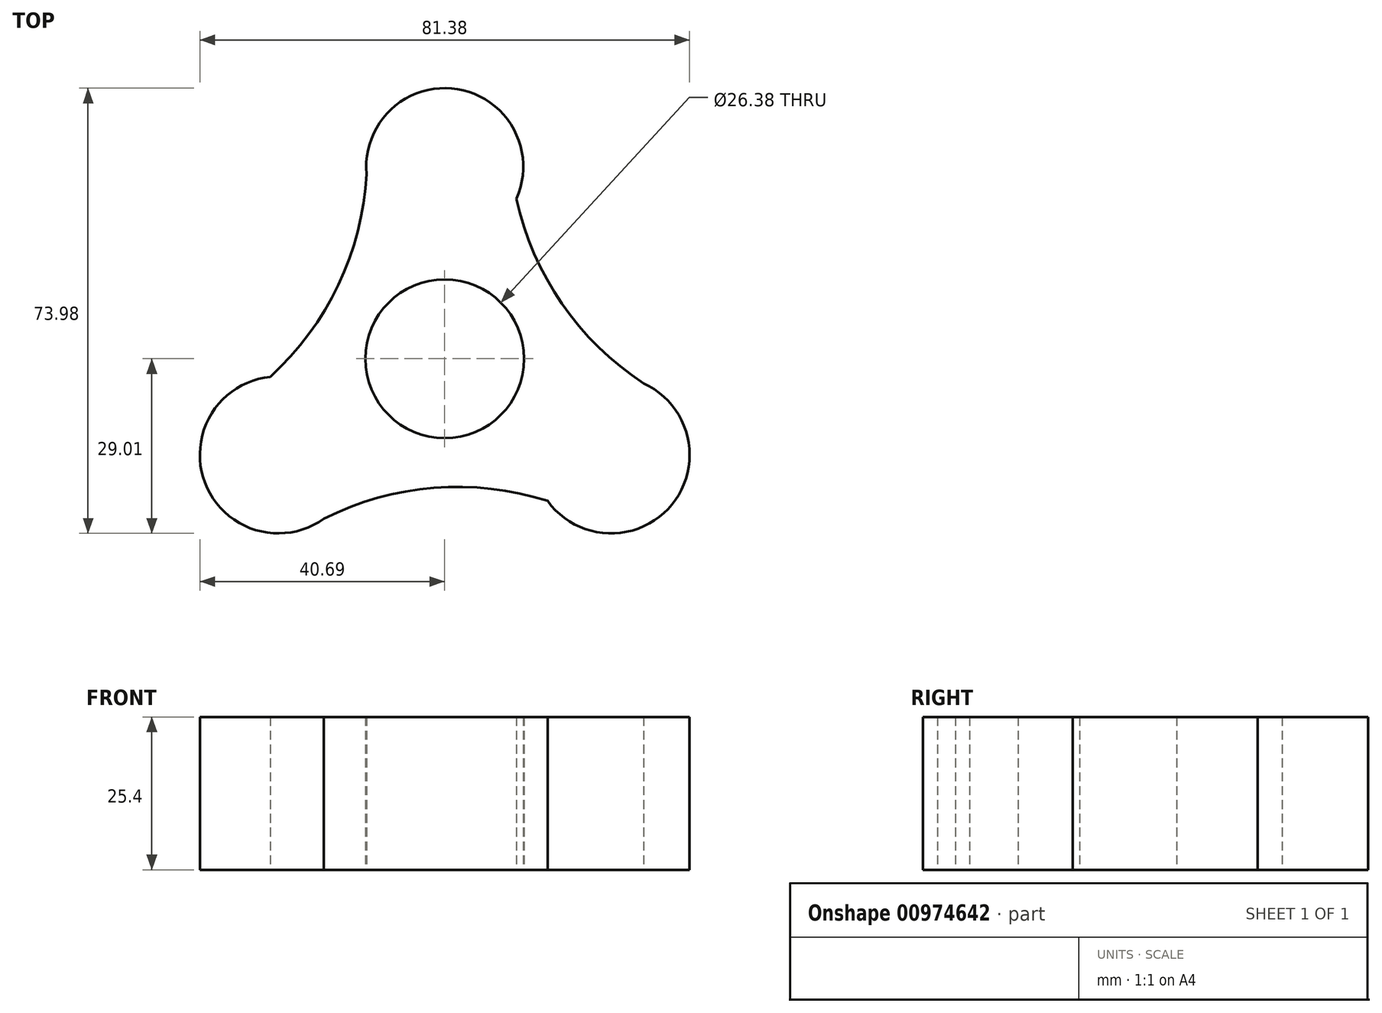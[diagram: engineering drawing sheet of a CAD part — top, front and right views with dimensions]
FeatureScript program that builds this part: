
annotation { "Feature Type Name" : "Feature", "Feature Type Description" : "" }
export const myFeature = defineFeature(function(context is Context, id is Id, definition is map)
    precondition{}
    {
        {
            var Q0;
            Q0=qCreatedBy(makeId("Top.planeOp"),FACE);
            var sketch = newSketch(context, id + "F0", { "sketchPlane" : qUnion([Q0])});
            skCircle(sketch, "E0", {"center": v(0, 0) * mm, "radius": 13.19 * mm});
            skArc(sketch, "E1", {"start": v(-30.05, -3.93) * mm, "mid": v(-17.45, 12.75) * mm, "end": v(-12.9, 33.15) * mm});
            skArc(sketch, "E2.1.0", {"start": v(18.43, -24.06) * mm, "mid": v(-2.31, -21.49) * mm, "end": v(-22.25, -27.75) * mm});
            skArc(sketch, "E2.2.0", {"start": v(11.62, 27.99) * mm, "mid": v(19.77, 8.74) * mm, "end": v(35.16, -5.4) * mm});
            skCircle(sketch, "E3", {"center": v(0, 31.93) * mm, "radius": 13.04 * mm});
            skCircle(sketch, "E4.1.0", {"center": v(-27.65, -15.97) * mm, "radius": 13.04 * mm});
            skCircle(sketch, "E4.2.0", {"center": v(27.65, -15.97) * mm, "radius": 13.04 * mm});
            skSolve(sketch);
        }
        {
            var Q0;
            Q0 = qSketchRegion(id + "F0", true);
            extrude(context, id + "F1", {"entities" : qUnion([Q0]), "depth" : 25.4 * mm, "offsetDistance" : 25.4 * mm});
        }
    });
